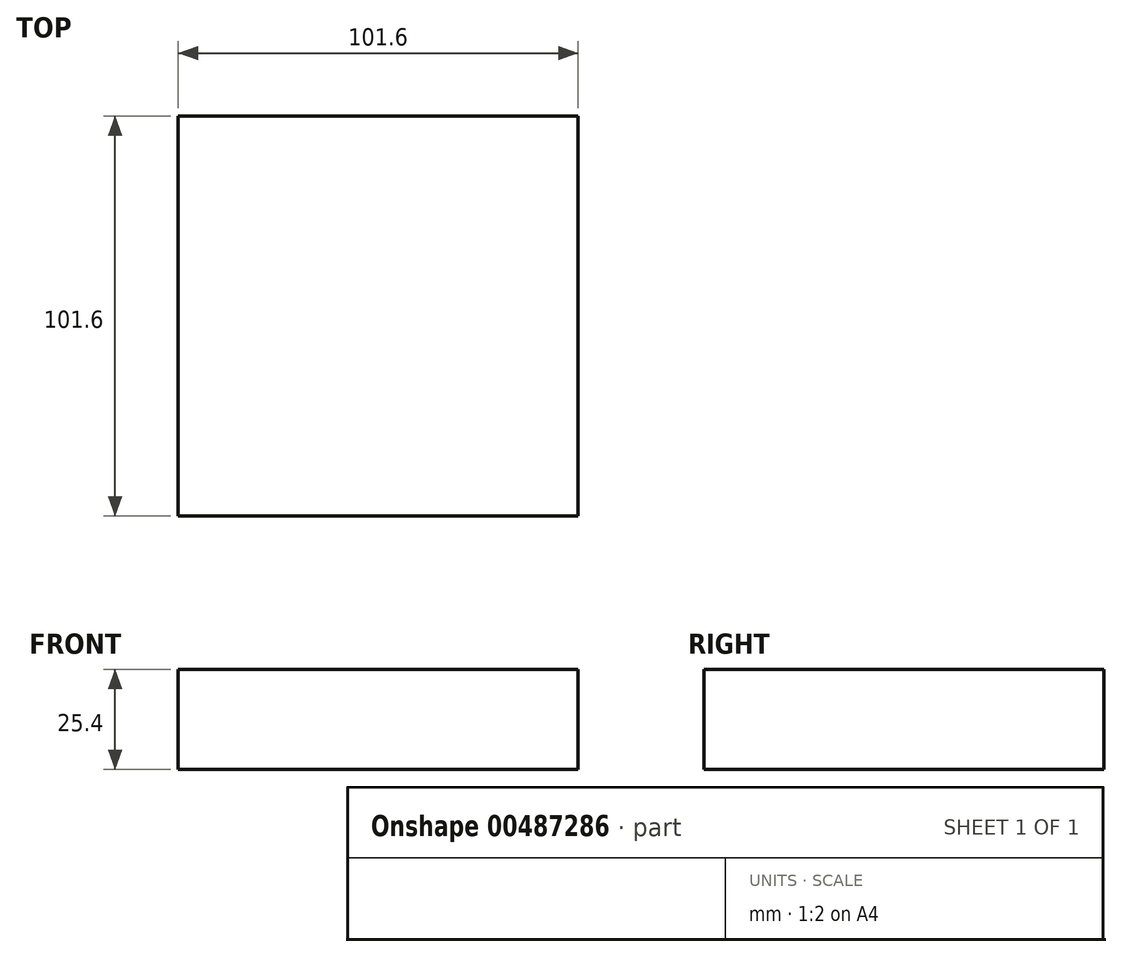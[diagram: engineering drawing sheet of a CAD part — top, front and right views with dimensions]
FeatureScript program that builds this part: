
annotation { "Feature Type Name" : "Feature", "Feature Type Description" : "" }
export const myFeature = defineFeature(function(context is Context, id is Id, definition is map)
    precondition{}
    {
        {
            var Q0;
            Q0=qCreatedBy(makeId("Top.planeOp"),FACE);
            var sketch = newSketch(context, id + "F0", { "sketchPlane" : qUnion([Q0])});
            skLineSegment(sketch, "E0.bottom", {"start": v(50.8, -50.8) * mm, "end": v(-50.8, -50.8) * mm});
            skLineSegment(sketch, "E0.top", {"start": v(50.8, 50.8) * mm, "end": v(-50.8, 50.8) * mm});
            skLineSegment(sketch, "E0.left", {"start": v(50.8, -50.8) * mm, "end": v(50.8, 50.8) * mm});
            skLineSegment(sketch, "E0.right", {"start": v(-50.8, -50.8) * mm, "end": v(-50.8, 50.8) * mm});
            skPoint(sketch, "E0.middle", {"position": v(0, 0) * mm});
            skSolve(sketch);
        }
        {
            var Q0;
            Q0 = qSketchRegion(id + "F0", true);
            extrude(context, id + "F1", {"entities" : qUnion([Q0]), "depth" : 25.4 * mm});
        }
    });
